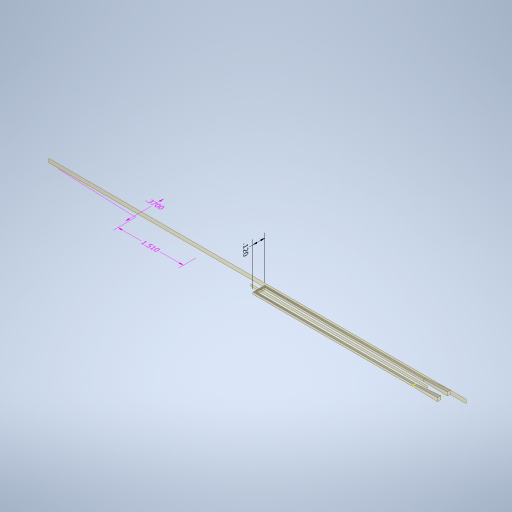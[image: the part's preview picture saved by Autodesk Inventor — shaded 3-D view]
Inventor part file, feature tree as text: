
AUTODESK INVENTOR PART (.ipt)
format: ipt  version: 2024.2 (Build 282272000, 272)  size: 310,272 bytes
history: native  units: in
note: dims shown in document units (in); Inventor stores cm internally (conversion verified against a paired STEP export)
features: other x5, plane x4, sketch x4, sweep x1, loft x1, mirror x1, projected_geometry x1
ambient origin geometry x8: Origin, YZ Plane, XZ Plane, XY Plane, X Axis, Y Axis, Z Axis, Center Point
bodies: Solid1 (feature_tree)
feature tree (17):
  other  "Annotations"
  sweep  "Sweep1"
  plane  "Work Plane1"
  plane  "Work Plane2"
  plane  "Work Plane4"
  sketch  "Sketch15"  dims[d86=-0.1175in]
  sketch  "Sketch16"  dims[d89=0.1in d90=0.0in d91=0.0in d92=0.0in d98=0.02in d99=0.02in d100=0.035in d102=0.035in d104=0.0in d109=0.0in d110=90.0deg d111=0.0in d112=90.0deg d116=-0.06in d113=0.0in d114=0.3937in d115=0.12in d42=0.2341in d43=0.169in d44=0.37in d48=0.2141in d49=0.2512in d50=1.51in]
  loft  "Loft3"
  plane  "Work Plane5"
  mirror  "Mirror3"
  sketch  "Sketch1"  dims[d6=0.0in d7=0.0in d11=0.25in d19=-0.25in]
  sketch  "Sketch2"  dims[d69=1.625in d70=1.625in]
  projected_geometry  "Projected Loop1"
  other  "Edges4"
  other  "Linear Dimension 1"
  other  "Linear Dimension 3"
  other  "Linear Dimension 4"
